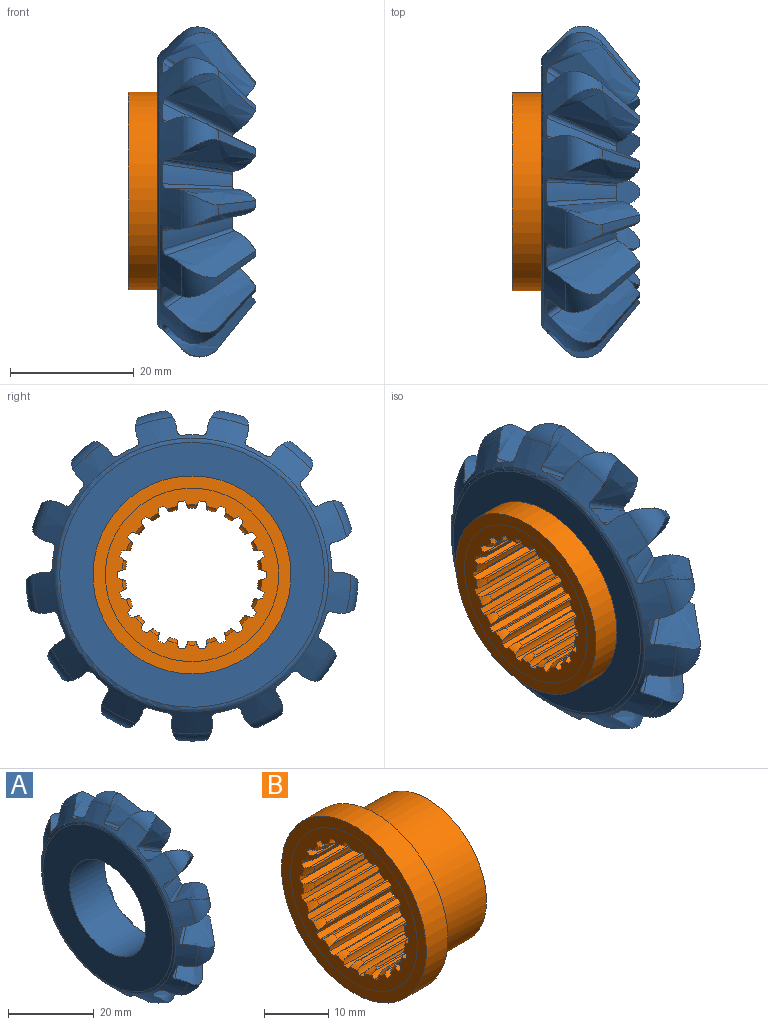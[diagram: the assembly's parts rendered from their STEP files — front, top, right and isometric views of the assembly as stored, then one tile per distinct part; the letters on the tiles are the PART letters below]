
ASSEMBLY  parts=2 mates=1
PART A: 98 faces, bbox 17.4x58.2x57.6 mm
  f0: cone r=13.5mm half-angle=45deg, axis (1,0,0), area 268.8mm2, adj f2,f3,f4,f5,f6,f7,f8,f15
  f1: cone r=28.83mm half-angle=45deg, axis (1,0,0), area 473.7mm2, adj f2,f3,f4,f5,f6,f7,f8,f9
  f2: bspline ~14.19x11.11mm, area 13.9mm2, adj f0,f1,f42,f90
  f3: bspline ~14.49x14.47mm, area 85.6mm2, adj f0,f1,f4,f12,f94
  f4: bspline ~14.19x10.1mm, area 13.9mm2, adj f0,f1,f3,f5
  f5: bspline ~12.78x9.5mm, area 35.8mm2, adj f0,f1,f4,f91
  f6: bspline ~14.47x10.77mm, area 85.6mm2, adj f0,f1,f7,f11,f95
  f7: bspline ~14.19x9.43mm, area 13.9mm2, adj f0,f1,f6,f92
  f8: bspline ~14.92x14.47mm, area 85.6mm2, adj f0,f1,f13,f28,f52
  f9: torus R=22.85mm, axis (1,0,0), area 25.4mm2, adj f1,f84,f88,f96
  f10: torus R=22.85mm, axis (1,0,0), area 27.3mm2, adj f1,f29,f40,f46
  f11: torus R=22.85mm, axis (1,0,0), area 27.3mm2, adj f1,f6,f34,f95
  f12: torus R=22.85mm, axis (1,0,0), area 27.3mm2, adj f1,f3,f42,f94
  f13: torus R=22.85mm, axis (1,0,0), area 27.3mm2, adj f1,f8,f52,f54
  f14: torus R=21.38mm, axis (1,0,0), area 107.4mm2, adj f1,f53
  f15: torus R=13.08mm, axis (-1,0,0), area 66.4mm2, adj f0,f93
  f16: torus R=22.85mm, axis (1,0,0), area 27.3mm2, adj f1,f30,f32,f66
  f17: torus R=22.85mm, axis (1,0,0), area 27.3mm2, adj f1,f44,f49,f65
  f18: torus R=22.85mm, axis (1,0,0), area 27.3mm2, adj f1,f48,f68,f72
  f19: torus R=22.85mm, axis (1,0,0), area 27.3mm2, adj f1,f24,f26,f47
  f20: torus R=22.85mm, axis (1,0,0), area 27.3mm2, adj f1,f36,f38,f45
  f21: torus R=22.85mm, axis (1,0,0), area 27.3mm2, adj f1,f27,f79,f83
  f22: torus R=22.85mm, axis (1,0,0), area 27.3mm2, adj f1,f31,f51,f55
  f23: torus R=22.85mm, axis (1,0,0), area 27.3mm2, adj f1,f41,f50,f61
  f24: bspline ~16.12x14.37mm, area 85.6mm2, adj f0,f1,f19,f47,f75
  f25: bspline ~14.19x11.11mm, area 13.9mm2, adj f0,f1,f65,f67
  f26: bspline ~14.47x13.85mm, area 85.6mm2, adj f0,f1,f19,f47,f74
  f27: cone r=17.85mm half-angle=51.2deg, axis (-1,0,0), area 13.5mm2, adj f0,f21,f79,f83
  f28: bspline ~14.19x10.67mm, area 13.9mm2, adj f0,f1,f8,f92
  f29: bspline ~15.12x14.47mm, area 85.6mm2, adj f0,f1,f10,f46,f77
  f30: bspline ~16.84x16.12mm, area 85.6mm2, adj f0,f1,f16,f32,f69
  f31: bspline ~16.61x16.12mm, area 85.6mm2, adj f0,f1,f22,f51,f59
  f32: cone r=17.85mm half-angle=51.2deg, axis (-1,0,0), area 13.5mm2, adj f0,f16,f30,f66
  f33: bspline ~12.78x10.14mm, area 35.8mm2, adj f0,f1,f75,f76
  f34: bspline ~16.12x13.35mm, area 85.6mm2, adj f0,f1,f11,f91,f95
  f35: bspline ~14.19x11.43mm, area 13.9mm2, adj f0,f1,f66,f67
  f36: bspline ~16.12x14.37mm, area 85.6mm2, adj f0,f1,f20,f39,f45
  f37: bspline ~11.18x8.81mm, area 35.8mm2, adj f0,f1,f59,f60
  f38: bspline ~14.47x13.85mm, area 85.6mm2, adj f0,f1,f20,f45,f80
  f39: bspline ~12.44x9.37mm, area 13.9mm2, adj f0,f1,f36,f78
  f40: bspline ~15.12x14.47mm, area 85.6mm2, adj f0,f1,f10,f46,f76
  f41: bspline ~14.47x10.77mm, area 85.6mm2, adj f0,f1,f23,f50,f60
  f42: bspline ~14.47x13.79mm, area 85.6mm2, adj f0,f1,f2,f12,f94
  f43: bspline ~11.18x8.14mm, area 35.8mm2, adj f0,f1,f73,f74
  f44: bspline ~16.14x16.12mm, area 85.6mm2, adj f0,f1,f17,f49,f63
  f45: cone r=17.85mm half-angle=51.2deg, axis (-1,0,0), area 13.5mm2, adj f0,f20,f36,f38
  f46: cone r=17.85mm half-angle=51.2deg, axis (-1,0,0), area 13.5mm2, adj f0,f10,f29,f40
  f47: cone r=17.85mm half-angle=51.2deg, axis (-1,0,0), area 13.5mm2, adj f0,f19,f24,f26
  f48: cone r=17.85mm half-angle=51.2deg, axis (-1,0,0), area 13.5mm2, adj f0,f18,f68,f72
  f49: cone r=17.85mm half-angle=51.2deg, axis (-1,0,0), area 13.5mm2, adj f0,f17,f44,f65
  f50: cone r=17.85mm half-angle=51.2deg, axis (-1,0,0), area 13.5mm2, adj f0,f23,f41,f61
  f51: cone r=17.85mm half-angle=51.2deg, axis (-1,0,0), area 13.5mm2, adj f0,f22,f31,f55
  f52: cone r=17.85mm half-angle=51.2deg, axis (-1,0,0), area 13.5mm2, adj f0,f8,f13,f54
  f53: plane 42.77x42.77mm, normal (-1,0,0), area 945.8mm2, adj f14,f97
  f54: bspline ~14.47x14.44mm, area 85.6mm2, adj f0,f1,f13,f52,f56
  f55: bspline ~14.47x14.44mm, area 85.6mm2, adj f0,f1,f22,f51,f57
  f56: bspline ~12.44x9.95mm, area 13.9mm2, adj f0,f1,f54,f58
  f57: bspline ~12.44x9.95mm, area 13.9mm2, adj f0,f1,f55,f58
  f58: bspline ~12.78x9.88mm, area 35.8mm2, adj f0,f1,f56,f57
  f59: bspline ~14.19x10.67mm, area 13.9mm2, adj f0,f1,f31,f37
  f60: bspline ~14.19x9.43mm, area 13.9mm2, adj f0,f1,f37,f41
  f61: bspline ~16.12x13.35mm, area 85.6mm2, adj f0,f1,f23,f50,f62
  f62: bspline ~14.19x8.63mm, area 13.9mm2, adj f0,f1,f61,f64
  f63: bspline ~14.19x10.1mm, area 13.9mm2, adj f0,f1,f44,f64
  f64: bspline ~12.78x9.5mm, area 35.8mm2, adj f0,f1,f62,f63
  f65: bspline ~14.47x13.79mm, area 85.6mm2, adj f0,f1,f17,f25,f49
  f66: bspline ~15.17x14.75mm, area 87.4mm2, adj f0,f1,f16,f32,f35
  f67: bspline ~11.18x8.85mm, area 35.8mm2, adj f0,f1,f25,f35
  f68: bspline ~14.47x11.88mm, area 85.6mm2, adj f0,f1,f18,f48,f70
  f69: bspline ~14.19x11.08mm, area 13.9mm2, adj f0,f1,f30,f71
  f70: bspline ~14.19x10.14mm, area 13.9mm2, adj f0,f1,f68,f71
  f71: bspline ~12.78x10.07mm, area 35.8mm2, adj f0,f1,f69,f70
  f72: bspline ~16.12x14.49mm, area 85.6mm2, adj f0,f1,f18,f48,f73
  f73: bspline ~14.19x8.52mm, area 13.9mm2, adj f0,f1,f43,f72
  f74: bspline ~14.19x9.38mm, area 13.9mm2, adj f0,f1,f26,f43
  f75: bspline ~12.44x9.37mm, area 13.9mm2, adj f0,f1,f24,f33
  f76: bspline ~14.19x11.34mm, area 13.9mm2, adj f0,f1,f33,f40
  f77: bspline ~14.19x11.34mm, area 13.9mm2, adj f0,f1,f29,f78
  f78: bspline ~12.78x10.14mm, area 35.8mm2, adj f0,f1,f39,f77
  f79: bspline ~16.12x14.49mm, area 85.6mm2, adj f0,f1,f21,f27,f81
  f80: bspline ~14.19x9.38mm, area 13.9mm2, adj f0,f1,f38,f82
  f81: bspline ~14.19x8.52mm, area 13.9mm2, adj f0,f1,f79,f82
  f82: bspline ~11.18x8.14mm, area 35.8mm2, adj f0,f1,f80,f81
  f83: bspline ~16.12x13.21mm, area 85.6mm2, adj f0,f1,f21,f27,f85
  f84: bspline ~15.13x14.47mm, area 85.6mm2, adj f0,f1,f9,f86,f96
  f85: bspline ~14.19x10.14mm, area 13.9mm2, adj f0,f1,f83,f87
  f86: bspline ~14.19x11.08mm, area 13.9mm2, adj f0,f1,f84,f87
  f87: bspline ~12.78x10.07mm, area 35.8mm2, adj f0,f1,f85,f86
  f88: bspline ~15.22x14.8mm, area 93.1mm2, adj f0,f1,f9,f89,f96
  f89: bspline ~14.19x11.43mm, area 13.9mm2, adj f0,f1,f88,f90
  f90: bspline ~11.18x8.85mm, area 35.8mm2, adj f0,f1,f2,f89
  f91: bspline ~14.19x8.63mm, area 13.9mm2, adj f0,f1,f5,f34
  f92: bspline ~11.18x8.81mm, area 35.8mm2, adj f0,f1,f7,f28
  f93: plane 26.17x26.17mm, normal (1,0,0), area 47mm2, adj f15,f97
  f94: cone r=17.85mm half-angle=51.2deg, axis (-1,0,0), area 13.5mm2, adj f0,f3,f12,f42
  f95: cone r=17.85mm half-angle=51.2deg, axis (-1,0,0), area 13.5mm2, adj f0,f6,f11,f34
  f96: cone r=17.85mm half-angle=51.2deg, axis (-1,0,0), area 13.5mm2, adj f0,f9,f84,f88
  f97: cylinder r=12.5mm len=25mm, axis (1,0,0), area 903.1mm2, adj f53,f93
PART B: 160 faces, bbox 16.7x32x32 mm
  f0: plane 26x26mm, normal (1,0,0), area 127.4mm2, adj f2,f3,f4,f5,f6,f7,f8,f9
  f1: plane 28x28mm, normal (-1,0,0), area 193.2mm2, adj f2,f3,f4,f5,f6,f7,f8,f9
  f2: cylinder r=12mm len=16.3mm, axis (1,0,0), area 16.3mm2, adj f0,f1,f67,f72
  f3: cylinder r=12mm len=16.3mm, axis (1,0,0), area 16.3mm2, adj f0,f1,f64,f69
  f4: cylinder r=12mm len=16.3mm, axis (1,0,0), area 16.3mm2, adj f0,f1,f61,f66
  f5: cylinder r=12mm len=16.3mm, axis (1,0,0), area 16.3mm2, adj f0,f1,f58,f63
  f6: cylinder r=12mm len=16.3mm, axis (1,0,0), area 16.3mm2, adj f0,f1,f55,f60
  f7: cylinder r=12mm len=16.3mm, axis (1,0,0), area 16.3mm2, adj f0,f1,f57,f153
  f8: cylinder r=12mm len=16.3mm, axis (1,0,0), area 16.3mm2, adj f0,f1,f54,f146
  f9: cylinder r=12mm len=16.3mm, axis (1,0,0), area 16.3mm2, adj f0,f1,f48,f52
  f10: cylinder r=12mm len=16.3mm, axis (1,0,0), area 16.3mm2, adj f0,f1,f45,f50
  f11: cylinder r=12mm len=16.3mm, axis (1,0,0), area 16.3mm2, adj f0,f1,f42,f47
  f12: cylinder r=12mm len=16.3mm, axis (1,0,0), area 16.3mm2, adj f0,f1,f39,f44
  f13: cylinder r=12mm len=16.3mm, axis (1,0,0), area 16.3mm2, adj f0,f1,f36,f41
  f14: cylinder r=12mm len=16.3mm, axis (1,0,0), area 16.3mm2, adj f0,f1,f33,f38
  f15: cylinder r=12mm len=16.3mm, axis (1,0,0), area 16.3mm2, adj f0,f1,f31,f35
  f16: cylinder r=12mm len=16.3mm, axis (1,0,0), area 16.3mm2, adj f0,f1,f29,f147
  f17: cylinder r=12mm len=16.3mm, axis (1,0,0), area 16.3mm2, adj f0,f1,f23,f149
  f18: cylinder r=12mm len=16.3mm, axis (1,0,0), area 16.3mm2, adj f0,f1,f25,f85
  f19: cylinder r=12mm len=16.3mm, axis (1,0,0), area 16.3mm2, adj f0,f1,f82,f87
  f20: cylinder r=12mm len=16.3mm, axis (1,0,0), area 16.3mm2, adj f0,f1,f79,f84
  f21: cylinder r=12mm len=16.3mm, axis (1,0,0), area 16.3mm2, adj f0,f1,f76,f81
  f22: cylinder r=12mm len=16.3mm, axis (1,0,0), area 16.3mm2, adj f0,f1,f73,f78
  f23: cylinder r=3.2mm len=16.3mm, axis (-1,0,0), area 18.4mm2, adj f0,f1,f17,f27,f28
  f24: cylinder r=10.75mm len=14.44mm, axis (-1,0,0), area 13.5mm2, adj f0,f26,f27,f28
  f25: cylinder r=3.2mm len=16.3mm, axis (-1,0,0), area 18.4mm2, adj f0,f1,f18,f26,f28
  f26: cylinder r=0.25mm len=15.55mm, axis (1,0,0), area 5mm2, adj f0,f24,f25,f28
  f27: cylinder r=0.25mm len=15.55mm, axis (1,0,0), area 5mm2, adj f0,f23,f24,f28
  f28: torus R=14mm, axis (-1,0,0), area 2.7mm2, adj f1,f23,f24,f25,f26,f27
  f29: cylinder r=3.2mm len=16.3mm, axis (-1,0,0), area 18.4mm2, adj f0,f1,f16,f88,f120
  f30: cylinder r=10.75mm len=14.44mm, axis (-1,0,0), area 13.5mm2, adj f0,f88,f120,f154
  f31: cylinder r=3.2mm len=16.3mm, axis (-1,0,0), area 18.4mm2, adj f0,f1,f15,f89,f121
  f32: cylinder r=10.75mm len=14.44mm, axis (-1,0,0), area 13.5mm2, adj f0,f89,f121,f152
  f33: cylinder r=3.2mm len=16.3mm, axis (-1,0,0), area 18.4mm2, adj f0,f1,f14,f90,f122
  f34: cylinder r=10.75mm len=14.44mm, axis (-1,0,0), area 13.5mm2, adj f0,f90,f122,f145
  f35: cylinder r=3.2mm len=16.3mm, axis (-1,0,0), area 18.4mm2, adj f0,f1,f15,f122,f145
  f36: cylinder r=3.2mm len=16.3mm, axis (-1,0,0), area 18.4mm2, adj f0,f1,f13,f91,f123
  f37: cylinder r=10.75mm len=14.44mm, axis (-1,0,0), area 13.5mm2, adj f0,f91,f123,f151
  f38: cylinder r=3.2mm len=16.3mm, axis (-1,0,0), area 18.4mm2, adj f0,f1,f14,f123,f151
  f39: cylinder r=3.2mm len=16.3mm, axis (-1,0,0), area 18.4mm2, adj f0,f1,f12,f92,f124
  f40: cylinder r=10.75mm len=14.44mm, axis (-1,0,0), area 13.5mm2, adj f0,f92,f124,f150
  f41: cylinder r=3.2mm len=16.3mm, axis (-1,0,0), area 18.4mm2, adj f0,f1,f13,f124,f150
  f42: cylinder r=3.2mm len=16.3mm, axis (-1,0,0), area 18.4mm2, adj f0,f1,f11,f125,f148
  f43: cylinder r=10.75mm len=14.44mm, axis (-1,0,0), area 13.5mm2, adj f0,f93,f125,f148
  f44: cylinder r=3.2mm len=16.3mm, axis (-1,0,0), area 18.4mm2, adj f0,f1,f12,f93,f125
  f45: cylinder r=3.2mm len=16.3mm, axis (-1,0,0), area 18.4mm2, adj f0,f1,f10,f126,f142
  f46: cylinder r=10.75mm len=14.44mm, axis (-1,0,0), area 13.5mm2, adj f0,f94,f126,f142
  f47: cylinder r=3.2mm len=16.3mm, axis (-1,0,0), area 18.4mm2, adj f0,f1,f11,f94,f126
  f48: cylinder r=3.2mm len=16.3mm, axis (-1,0,0), area 18.4mm2, adj f0,f1,f9,f127,f144
  f49: cylinder r=10.75mm len=14.44mm, axis (-1,0,0), area 13.5mm2, adj f0,f95,f127,f144
  f50: cylinder r=3.2mm len=16.3mm, axis (-1,0,0), area 18.4mm2, adj f0,f1,f10,f95,f127
  f51: cylinder r=10.75mm len=14.44mm, axis (-1,0,0), area 13.5mm2, adj f0,f96,f128,f143
  f52: cylinder r=3.2mm len=16.3mm, axis (-1,0,0), area 18.4mm2, adj f0,f1,f9,f96,f128
  f53: cylinder r=10.75mm len=14.44mm, axis (-1,0,0), area 13.5mm2, adj f0,f97,f129,f141
  f54: cylinder r=3.2mm len=16.3mm, axis (-1,0,0), area 18.4mm2, adj f0,f1,f8,f97,f129
  f55: cylinder r=3.2mm len=16.3mm, axis (-1,0,0), area 18.4mm2, adj f0,f1,f6,f99,f130
  f56: cylinder r=10.75mm len=14.44mm, axis (-1,0,0), area 13.5mm2, adj f0,f98,f99,f130
  f57: cylinder r=3.2mm len=16.3mm, axis (-1,0,0), area 18.4mm2, adj f0,f1,f7,f98,f130
  f58: cylinder r=3.2mm len=16.3mm, axis (-1,0,0), area 18.4mm2, adj f0,f1,f5,f101,f131
  f59: cylinder r=10.75mm len=14.44mm, axis (-1,0,0), area 13.5mm2, adj f0,f100,f101,f131
  f60: cylinder r=3.2mm len=16.3mm, axis (-1,0,0), area 18.4mm2, adj f0,f1,f6,f100,f131
  f61: cylinder r=3.2mm len=16.3mm, axis (-1,0,0), area 18.4mm2, adj f0,f1,f4,f103,f132
  f62: cylinder r=10.75mm len=14.44mm, axis (-1,0,0), area 13.5mm2, adj f0,f102,f103,f132
  f63: cylinder r=3.2mm len=16.3mm, axis (-1,0,0), area 18.4mm2, adj f0,f1,f5,f102,f132
  f64: cylinder r=3.2mm len=16.3mm, axis (-1,0,0), area 18.4mm2, adj f0,f1,f3,f105,f133
  f65: cylinder r=10.75mm len=14.44mm, axis (-1,0,0), area 13.5mm2, adj f0,f104,f105,f133
  f66: cylinder r=3.2mm len=16.3mm, axis (-1,0,0), area 18.4mm2, adj f0,f1,f4,f104,f133
  f67: cylinder r=3.2mm len=16.3mm, axis (-1,0,0), area 18.4mm2, adj f0,f1,f2,f107,f134
  f68: cylinder r=10.75mm len=14.44mm, axis (-1,0,0), area 13.5mm2, adj f0,f106,f107,f134
  f69: cylinder r=3.2mm len=16.3mm, axis (-1,0,0), area 18.4mm2, adj f0,f1,f3,f106,f134
  f70: cylinder r=3.2mm len=16.3mm, axis (-1,0,0), area 18.4mm2, adj f0,f1,f109,f135,f155
  f71: cylinder r=10.75mm len=14.44mm, axis (-1,0,0), area 13.5mm2, adj f0,f108,f109,f135
  f72: cylinder r=3.2mm len=16.3mm, axis (-1,0,0), area 18.4mm2, adj f0,f1,f2,f108,f135
  f73: cylinder r=3.2mm len=16.3mm, axis (-1,0,0), area 18.4mm2, adj f0,f1,f22,f111,f136
  f74: cylinder r=10.75mm len=14.44mm, axis (-1,0,0), area 13.5mm2, adj f0,f110,f111,f136
  f75: cylinder r=3.2mm len=16.3mm, axis (-1,0,0), area 18.4mm2, adj f0,f1,f110,f136,f155
  f76: cylinder r=3.2mm len=16.3mm, axis (-1,0,0), area 18.4mm2, adj f0,f1,f21,f113,f137
  f77: cylinder r=10.75mm len=14.44mm, axis (-1,0,0), area 13.5mm2, adj f0,f112,f113,f137
  f78: cylinder r=3.2mm len=16.3mm, axis (-1,0,0), area 18.4mm2, adj f0,f1,f22,f112,f137
  f79: cylinder r=3.2mm len=16.3mm, axis (-1,0,0), area 18.4mm2, adj f0,f1,f20,f115,f138
  f80: cylinder r=10.75mm len=14.44mm, axis (-1,0,0), area 13.5mm2, adj f0,f114,f115,f138
  f81: cylinder r=3.2mm len=16.3mm, axis (-1,0,0), area 18.4mm2, adj f0,f1,f21,f114,f138
  f82: cylinder r=3.2mm len=16.3mm, axis (-1,0,0), area 18.4mm2, adj f0,f1,f19,f117,f139
  f83: cylinder r=10.75mm len=14.44mm, axis (-1,0,0), area 13.5mm2, adj f0,f116,f117,f139
  f84: cylinder r=3.2mm len=16.3mm, axis (-1,0,0), area 18.4mm2, adj f0,f1,f20,f116,f139
  f85: cylinder r=3.2mm len=16.3mm, axis (-1,0,0), area 18.4mm2, adj f0,f1,f18,f119,f140
  f86: cylinder r=10.75mm len=14.44mm, axis (-1,0,0), area 13.5mm2, adj f0,f118,f119,f140
  f87: cylinder r=3.2mm len=16.3mm, axis (-1,0,0), area 18.4mm2, adj f0,f1,f19,f118,f140
  f88: cylinder r=0.25mm len=15.55mm, axis (1,0,0), area 5mm2, adj f0,f29,f30,f120
  f89: cylinder r=0.25mm len=15.55mm, axis (1,0,0), area 5mm2, adj f0,f31,f32,f121
  f90: cylinder r=0.25mm len=15.55mm, axis (1,0,0), area 5mm2, adj f0,f33,f34,f122
  f91: cylinder r=0.25mm len=15.55mm, axis (1,0,0), area 5mm2, adj f0,f36,f37,f123
  f92: cylinder r=0.25mm len=15.55mm, axis (1,0,0), area 5mm2, adj f0,f39,f40,f124
  f93: cylinder r=0.25mm len=15.55mm, axis (1,0,0), area 5mm2, adj f0,f43,f44,f125
  f94: cylinder r=0.25mm len=15.55mm, axis (1,0,0), area 5mm2, adj f0,f46,f47,f126
  f95: cylinder r=0.25mm len=15.55mm, axis (1,0,0), area 5mm2, adj f0,f49,f50,f127
  f96: cylinder r=0.25mm len=15.55mm, axis (1,0,0), area 5mm2, adj f0,f51,f52,f128
  f97: cylinder r=0.25mm len=15.55mm, axis (1,0,0), area 5mm2, adj f0,f53,f54,f129
  f98: cylinder r=0.25mm len=15.55mm, axis (1,0,0), area 5mm2, adj f0,f56,f57,f130
  f99: cylinder r=0.25mm len=15.55mm, axis (1,0,0), area 5mm2, adj f0,f55,f56,f130
  f100: cylinder r=0.25mm len=15.55mm, axis (1,0,0), area 5mm2, adj f0,f59,f60,f131
  f101: cylinder r=0.25mm len=15.55mm, axis (1,0,0), area 5mm2, adj f0,f58,f59,f131
  f102: cylinder r=0.25mm len=15.55mm, axis (1,0,0), area 5mm2, adj f0,f62,f63,f132
  f103: cylinder r=0.25mm len=15.55mm, axis (1,0,0), area 5mm2, adj f0,f61,f62,f132
  f104: cylinder r=0.25mm len=15.55mm, axis (1,0,0), area 5mm2, adj f0,f65,f66,f133
  f105: cylinder r=0.25mm len=15.55mm, axis (1,0,0), area 5mm2, adj f0,f64,f65,f133
  f106: cylinder r=0.25mm len=15.55mm, axis (1,0,0), area 5mm2, adj f0,f68,f69,f134
  f107: cylinder r=0.25mm len=15.55mm, axis (1,0,0), area 5mm2, adj f0,f67,f68,f134
  f108: cylinder r=0.25mm len=15.55mm, axis (1,0,0), area 5mm2, adj f0,f71,f72,f135
  f109: cylinder r=0.25mm len=15.55mm, axis (1,0,0), area 5mm2, adj f0,f70,f71,f135
  f110: cylinder r=0.25mm len=15.55mm, axis (1,0,0), area 5mm2, adj f0,f74,f75,f136
  f111: cylinder r=0.25mm len=15.55mm, axis (1,0,0), area 5mm2, adj f0,f73,f74,f136
  f112: cylinder r=0.25mm len=15.55mm, axis (1,0,0), area 5mm2, adj f0,f77,f78,f137
  f113: cylinder r=0.25mm len=15.55mm, axis (1,0,0), area 5mm2, adj f0,f76,f77,f137
  f114: cylinder r=0.25mm len=15.55mm, axis (1,0,0), area 5mm2, adj f0,f80,f81,f138
  f115: cylinder r=0.25mm len=15.55mm, axis (1,0,0), area 5mm2, adj f0,f79,f80,f138
  f116: cylinder r=0.25mm len=15.55mm, axis (1,0,0), area 5mm2, adj f0,f83,f84,f139
  f117: cylinder r=0.25mm len=15.55mm, axis (1,0,0), area 5mm2, adj f0,f82,f83,f139
  f118: cylinder r=0.25mm len=15.55mm, axis (1,0,0), area 5mm2, adj f0,f86,f87,f140
  f119: cylinder r=0.25mm len=15.55mm, axis (1,0,0), area 5mm2, adj f0,f85,f86,f140
  f120: torus R=14mm, axis (-1,0,0), area 2.7mm2, adj f1,f29,f30,f88,f149,f154
  f121: torus R=14mm, axis (-1,0,0), area 2.7mm2, adj f1,f31,f32,f89,f147,f152
  f122: torus R=14mm, axis (-1,0,0), area 2.7mm2, adj f1,f33,f34,f35,f90,f145
  f123: torus R=14mm, axis (-1,0,0), area 2.7mm2, adj f1,f36,f37,f38,f91,f151
  f124: torus R=14mm, axis (-1,0,0), area 2.7mm2, adj f1,f39,f40,f41,f92,f150
  f125: torus R=14mm, axis (-1,0,0), area 2.7mm2, adj f1,f42,f43,f44,f93,f148
  f126: torus R=14mm, axis (-1,0,0), area 2.7mm2, adj f1,f45,f46,f47,f94,f142
  f127: torus R=14mm, axis (-1,0,0), area 2.7mm2, adj f1,f48,f49,f50,f95,f144
  f128: torus R=14mm, axis (-1,0,0), area 2.7mm2, adj f1,f51,f52,f96,f143,f146
  f129: torus R=14mm, axis (-1,0,0), area 2.7mm2, adj f1,f53,f54,f97,f141,f153
  f130: torus R=14mm, axis (-1,0,0), area 2.7mm2, adj f1,f55,f56,f57,f98,f99
  f131: torus R=14mm, axis (-1,0,0), area 2.7mm2, adj f1,f58,f59,f60,f100,f101
  f132: torus R=14mm, axis (-1,0,0), area 2.7mm2, adj f1,f61,f62,f63,f102,f103
  f133: torus R=14mm, axis (-1,0,0), area 2.7mm2, adj f1,f64,f65,f66,f104,f105
  f134: torus R=14mm, axis (-1,0,0), area 2.7mm2, adj f1,f67,f68,f69,f106,f107
  f135: torus R=14mm, axis (-1,0,0), area 2.7mm2, adj f1,f70,f71,f72,f108,f109
  f136: torus R=14mm, axis (-1,0,0), area 2.7mm2, adj f1,f73,f74,f75,f110,f111
  f137: torus R=14mm, axis (-1,0,0), area 2.7mm2, adj f1,f76,f77,f78,f112,f113
  f138: torus R=14mm, axis (-1,0,0), area 2.7mm2, adj f1,f79,f80,f81,f114,f115
  f139: torus R=14mm, axis (-1,0,0), area 2.7mm2, adj f1,f82,f83,f84,f116,f117
  f140: torus R=14mm, axis (-1,0,0), area 2.7mm2, adj f1,f85,f86,f87,f118,f119
  f141: cylinder r=0.25mm len=15.55mm, axis (1,0,0), area 5mm2, adj f0,f53,f129,f153
  f142: cylinder r=0.25mm len=15.55mm, axis (1,0,0), area 5mm2, adj f0,f45,f46,f126
  f143: cylinder r=0.25mm len=15.55mm, axis (1,0,0), area 5mm2, adj f0,f51,f128,f146
  f144: cylinder r=0.25mm len=15.55mm, axis (1,0,0), area 5mm2, adj f0,f48,f49,f127
  f145: cylinder r=0.25mm len=15.55mm, axis (1,0,0), area 5mm2, adj f0,f34,f35,f122
  f146: cylinder r=3.2mm len=16.3mm, axis (-1,0,0), area 18.4mm2, adj f0,f1,f8,f128,f143
  f147: cylinder r=3.2mm len=16.3mm, axis (-1,0,0), area 18.4mm2, adj f0,f1,f16,f121,f152
  f148: cylinder r=0.25mm len=15.55mm, axis (1,0,0), area 5mm2, adj f0,f42,f43,f125
  f149: cylinder r=3.2mm len=16.3mm, axis (-1,0,0), area 18.4mm2, adj f0,f1,f17,f120,f154
  f150: cylinder r=0.25mm len=15.55mm, axis (1,0,0), area 5mm2, adj f0,f40,f41,f124
  f151: cylinder r=0.25mm len=15.55mm, axis (1,0,0), area 5mm2, adj f0,f37,f38,f123
  f152: cylinder r=0.25mm len=15.55mm, axis (1,0,0), area 5mm2, adj f0,f32,f121,f147
  f153: cylinder r=3.2mm len=16.3mm, axis (-1,0,0), area 18.4mm2, adj f0,f1,f7,f129,f141
  f154: cylinder r=0.25mm len=15.55mm, axis (1,0,0), area 5mm2, adj f0,f30,f120,f149
  f155: cylinder r=12mm len=16.3mm, axis (1,0,0), area 16.3mm2, adj f0,f1,f70,f75
  f156: plane 32x32mm, normal (-1,0,0), area 188.1mm2, adj f1,f157
  f157: cylinder r=16mm len=32mm, axis (1,0,0), area 482.5mm2, adj f156,f159
  f158: cylinder r=13mm len=26mm, axis (-1,0,0), area 939.3mm2, adj f0,f159
  f159: plane 32x32mm, normal (1,0,0), area 273.3mm2, adj f157,f158
PLACE A t=(-11.5,-0.15,0.01)mm
PLACE B t=(-11.5,-0.15,0.01)mm
MATE cylindrical A.f0 <-> B.f158  axis (1,0,0) through (-5.75,-0.15,0.01)mm
